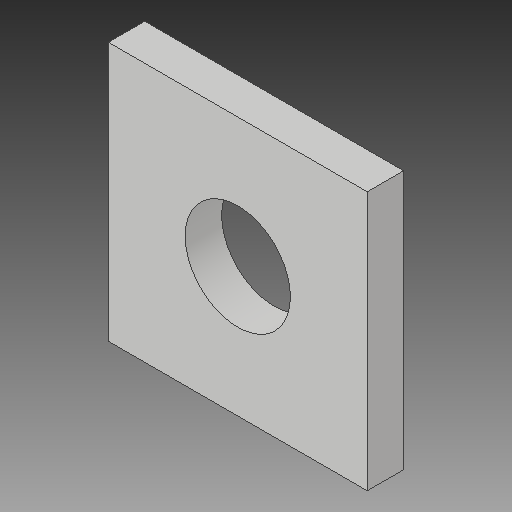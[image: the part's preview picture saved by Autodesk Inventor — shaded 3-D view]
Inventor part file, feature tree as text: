
AUTODESK INVENTOR PART (.ipt)
format: ipt  version: 2018 (Build 220112000, 112)  size: 95,744 bytes
history: native  units: mm
features: sketch x2, other x1, extrude x1, hole x1
ambient origin geometry x8: Origin, YZ Plane, XZ Plane, XY Plane, X Axis, Y Axis, Z Axis, Center Point
bodies: Body1 (feature_tree)
feature tree (5):
  other  "ソリッド1"
  extrude  "押し出し1"  Depth=32.0mm
  hole  "穴1"  [1 undecoded]
  sketch  "スケッチ1"
  sketch  "スケッチ2"
note: 1 required parameter value undecoded (feature->parameter linkage not recoverable at this tier; creation-order binding heuristic only, values carry confidence <= 0.55)
